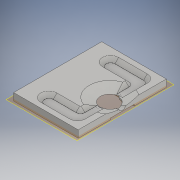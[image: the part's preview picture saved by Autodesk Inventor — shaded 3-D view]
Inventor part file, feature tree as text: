
AUTODESK INVENTOR PART (.ipt)
format: ipt  version: 2016 (Build 200138000, 138)  size: 242,176 bytes
history: native  units: mm
features: extrude x5, sketch x5, plane x3, other x2, chamfer x2, mirror x2, projected_geometry x2, loft x1
ambient origin geometry x8: Origin, YZ Plane, XZ Plane, XY Plane, X Axis, Y Axis, Z Axis, Center Point
bodies: Solid1 (feature_tree)
feature tree (22):
  extrude  "Extrusion1"  Depth=44.0mm
  other  "droso_bath"
  sketch  "Sketch3"  dims[d0=60.0mm d1=44.0mm]
  extrude  "Extrusion2"  Depth=2.5mm
  chamfer  "Chamfer1"  Distance=4.0mm
  extrude  "Extrusion6"  Depth=6.0mm
  chamfer  "Chamfer3"  Distance=2.0mm
  mirror  "Mirror3"
  plane  "Work Plane1"
  extrude  "Extrusion9"  Depth=2.5mm
  mirror  "Mirror5"
  extrude  "Extrusion13"  Depth=2.5mm
  sketch  "Sketch12"  dims[d5=12.0mm d14=4.0mm d15=0.0mm]
  plane  "Work Plane2"
  loft  "Loft1"
  plane  "Work Plane3"
  other  "base_rect"
  sketch  "Sketch11"  dims[d2=4.0mm d3=0.0mm d4=2.5mm]
  projected_geometry  "Projected Loop7"
  projected_geometry  "Projected Loop8"
  sketch  "Sketch13"  dims[d16=8.0mm d17=2.0mm d18=3.490659mm d32=6.0mm]
  sketch  "Sketch14"  dims[d33=6.0mm d34=2.0mm d35=12.0mm d36=3.0mm d38=2.6mm d39=0.0mm d42=2.5mm d43=2.0mm d44=30.0deg d66=8.0mm d67=60.0deg d68=1.0mm d69=0.0mm d86=1.0mm d87=0.0mm d88=-8.0mm d89=3.0mm d90=5.0mm d91=0.0mm d92=90.0deg d93=0.0mm d94=90.0deg d96=2.6mm]
